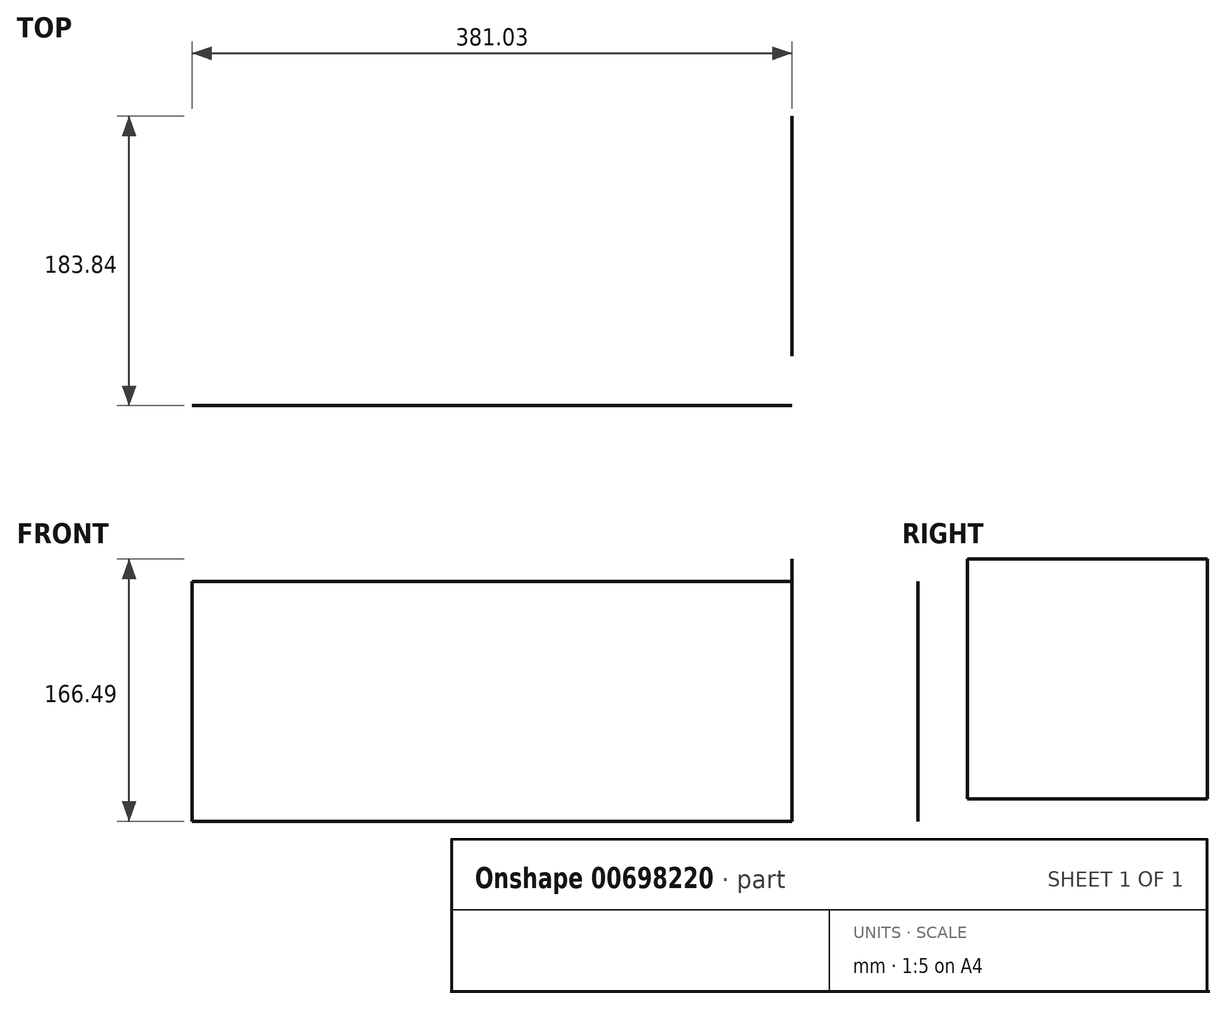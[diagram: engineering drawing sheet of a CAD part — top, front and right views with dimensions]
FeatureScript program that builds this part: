
annotation { "Feature Type Name" : "Feature", "Feature Type Description" : "" }
export const myFeature = defineFeature(function(context is Context, id is Id, definition is map)
    precondition{}
    {
        {
            var Q0;
            Q0=qCreatedBy(makeId("Front.planeOp"),FACE);
            var sketch = newSketch(context, id + "F0", { "sketchPlane" : qUnion([Q0])});
            skLineSegment(sketch, "E0.bottom", {"start": v(-381, -67.76) * mm, "end": v(0, -67.76) * mm});
            skLineSegment(sketch, "E0.top", {"start": v(-381, 84.64) * mm, "end": v(0, 84.64) * mm});
            skLineSegment(sketch, "E0.left", {"start": v(-381, -67.76) * mm, "end": v(-381, 84.64) * mm});
            skLineSegment(sketch, "E0.right", {"start": v(0, -67.76) * mm, "end": v(0, 84.64) * mm});
            skSolve(sketch);
        }
        {
            var Q0;
            Q0=qCreatedBy(makeId("Right.planeOp"),FACE);
            var sketch = newSketch(context, id + "F1", { "sketchPlane" : qUnion([Q0])});
            skLineSegment(sketch, "E1.bottom", {"start": v(31.4, 98.73) * mm, "end": v(183.8, 98.73) * mm});
            skLineSegment(sketch, "E1.top", {"start": v(31.4, -53.67) * mm, "end": v(183.8, -53.67) * mm});
            skLineSegment(sketch, "E1.left", {"start": v(31.4, 98.73) * mm, "end": v(31.4, -53.67) * mm});
            skLineSegment(sketch, "E1.right", {"start": v(183.8, 98.73) * mm, "end": v(183.8, -53.67) * mm});
            skSolve(sketch);
        }
        {
            var Q0;
            Q0=makeQuery(id+"F1.imprint","IMPRINT",FACE,{"disambiguationData":[TD([[makeQuery(id+"F1.imprint","IMPRINT",EDGE,{"derivedFrom":sQuery(id+"F1.wireOp",EDGE,"E1.bottom")}),-1.0]])]});
            extrude(context, id + "F2", {"entities" : qUnion([Q0]), "depth" : 3 / 101.6 * mm, "offsetDistance" : 25.4 * mm});
        }
        {
            var Q0;
            Q0=makeQuery(id+"F0.imprint","IMPRINT",FACE,{"disambiguationData":[TD([[makeQuery(id+"F0.imprint","IMPRINT",EDGE,{"derivedFrom":sQuery(id+"F0.wireOp",EDGE,"E0.bottom")}),1.0]])]});
            extrude(context, id + "F3", {"entities" : qUnion([Q0]), "depth" : 3 / 101.6 * mm, "offsetDistance" : 25.4 * mm});
        }
    });
